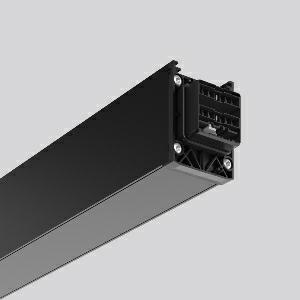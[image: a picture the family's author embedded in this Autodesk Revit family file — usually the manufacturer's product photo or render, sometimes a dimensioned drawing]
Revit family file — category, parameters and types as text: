
# Revit family: linedo_0_6m_00_0_950600_003_700_900_4d21
name_source: partatom
category: Lighting Fixtures
units: mm (PartAtom-declared; Revit-internal decimal feet)

## family parameters
Cut with Voids When Loaded = No
Host = Face
Light Source = No
Part Type = Normal
Room Calculation Point = No
Round Connector Dimension = Use Diameter
Shared = No

## types (1)
- LINEDO_0,6m_00_0
    Apparent Load = 0 VA
    Default Elevation = 1800 mm
    Description = Series: LINEDO
Rapid-installation complete module for universal use as a continuous line luminaire. Blank module. System profile made of aluminium extrusion profile, powder-coated. Cover made of plastic, surface like housing. Simple, tool-free installation of system profiles using separate accessories for cable, chain or ceiling suspension. Tool-free connection and mechanical connectors to secure. Please order supply module, connection and mounting accessories separately. Luminaire with limited surface temperature in accordance with EN  60598-2-24 for use in environments in which a deposit of non-conductive dust on the luminaire can be expected. 
Colour: deep black, matt (RAL 9005)
Length: 598 mm
Width: 58 mm
Height: 76 mm
Weight: 1,08 kg
Type of Installation: Ceiling mounting, Suspension cable/chain
    Height = 76 mm
    Lamp = 0 x
    Length = 598 mm
    Luminous efficacy = 0 lm/W
    Manufacturer = RZB
    ModVariant = No
    Model = 950600.003.700.900
    Mounting Place = Ceiling
    Mounting Type = Pendant, Surface mounted
    Number of Poles = 1
    OnlyDefault = Yes
    Power Factor = 1
    Product Name = LINEDO_0,6m_00_0
    Product group = Surface mounted continuous line luminaire system
    ProductGroupID = 310
    Protection Class = Protection class I
    Protection Degree = IP 54
    RLX_Detail_Level = 1
    RLX_Emergency_Light_Flux = 0 lm
    RLX_Emergency_Type = 0
    RLX_Emergency_Type_DB = No
    RlxData = <blob elided: 33929 chars, md5=07c4a451>
    Standby Power = 0 W
    System Light Flux = 0 lm
    System Power = 0 W
    Type Comments = Product without accessories
    Type Image = 954500.003.400.900.jpg
    URL = http://relux.com
    VarID = ---
    Voltage = 230 V
    Voltage Range = 220-240 V
    Weight = 0.00 kg
    Width = 58 mm

## geometry (parser evidence)
native form markers: Blend x4, Sweep x12
no freeform markers — native parametric forms only
